# Revit family: Trane_TVR_Indoor_Floor standing_4TVN0012(15)EF000AA(2nd DC)
name_source: partatom
category: Equipamento mecânico
units: mm (PartAtom-declared; Revit-internal decimal feet)

## family parameters
Com base no plano de trabalho = Não
Compartilhado = Não
Corte com vazios quando carregada = Não
Cota do conector redondo = Utilizar diâmetro
Número OmniClass = 23.75.00.00
Ponto de cálculo do ambiente = Não
Sempre na vertical = Sim
Tipo de parte = Normal
Título OmniClass = Climate Control (HVAC)

## types (2) — shared parameters
Condensation = air
Depth = 220  [stored 0.721785 ft]
Descrição = High efficiency air cooled
Fabricante = Trane
Gas = R410a
Gas pipe = 12.7  [stored 0.0416667 ft]
Height = 596  [stored 1.95538 ft]
Installation = Indoor installation
Liquid pipe = 6.35  [stored 0.0208333 ft]
MFA (Maximum Fuse Amps) = 15 A
Machine material = Galvanized Steel
Net Weight = 33.00 kg
Panel color = S1004
Series = TVR ULTRA
URL = https://www.trane.com
Width = 1200

## per-type parameters (varying)
| type | Air  Flow | Cooling Capacity | Cooling Power Input | Heating Capacity | Heating Power Input | MCA (Minimum Circuit Amps) | Power supply |
| 4TVN0012EF000AA | 624/591/557/522/473/420/375 m3/h | 4 kW | 55 W | 4 kW | 55 W | 0 A | 220-240V ~50/60Hz |
| 4TVN0015EF000AA | 660/625/583/542/501/475/440 m3/h | 5 kW | 60 W | 5 kW | 60 W | 1 A | 220-240V ~50Hz |

note: column(s) folded — value = type name in every type: Modelo

note: [stored X ft] marks values corroborated as IEEE doubles in the binary element streams (Revit-internal decimal feet)
